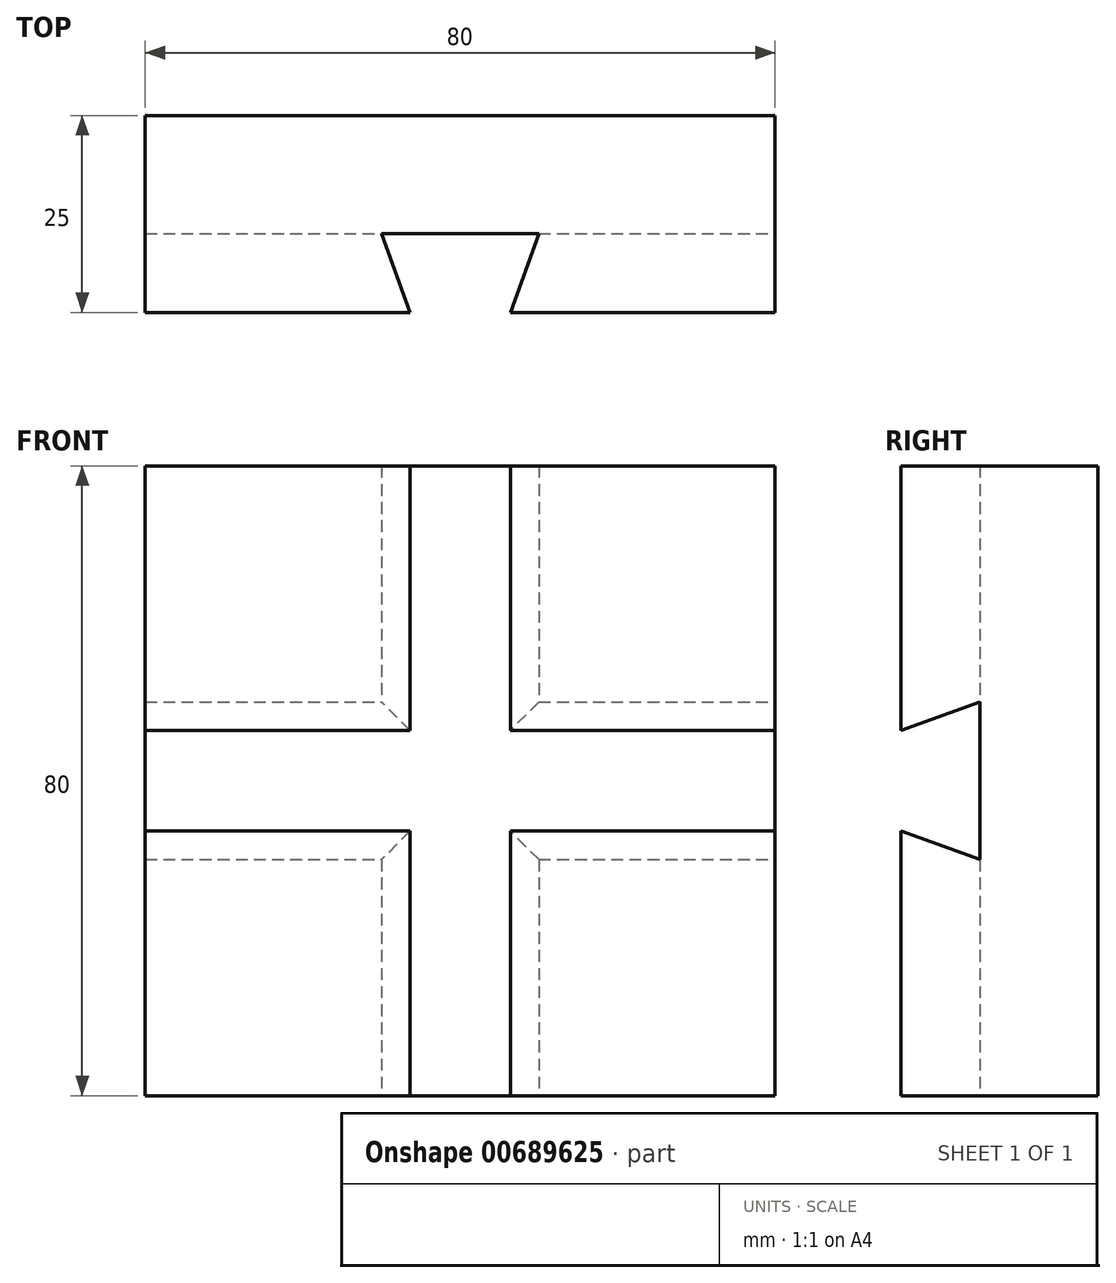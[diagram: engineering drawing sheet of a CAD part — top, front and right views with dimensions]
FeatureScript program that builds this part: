
annotation { "Feature Type Name" : "Feature", "Feature Type Description" : "" }
export const myFeature = defineFeature(function(context is Context, id is Id, definition is map)
    precondition{}
    {
        {
            var Q0;
            Q0=qCreatedBy(makeId("Front.planeOp"),FACE);
            var sketch = newSketch(context, id + "F0", { "sketchPlane" : qUnion([Q0])});
            skLineSegment(sketch, "E0.bottom", {"start": v(0, 0) * mm, "end": v(-80, 0) * mm});
            skLineSegment(sketch, "E0.top", {"start": v(0, 80) * mm, "end": v(-80, 80) * mm});
            skLineSegment(sketch, "E0.left", {"start": v(0, 0) * mm, "end": v(0, 80) * mm});
            skLineSegment(sketch, "E0.right", {"start": v(-80, 0) * mm, "end": v(-80, 80) * mm});
            skLineSegment(sketch, "E1", {"start": v(0, 0) * mm, "end": v(0, 33.64) * mm});
            skSolve(sketch);
        }
        {
            var Q0;
            Q0=makeQuery(id+"F0.imprint","IMPRINT",FACE,{"disambiguationData":[TD([[makeQuery(id+"F0.imprint","IMPRINT",EDGE,{"derivedFrom":sQuery(id+"F0.wireOp",EDGE,"E0.bottom")}),-1.0]])]});
            extrude(context, id + "F1", {"entities" : qUnion([Q0]), "depth" : 25 * mm, "offsetDistance" : 25 * mm});
        }
        {
            var Q0;
            Q0=makeQuery(id+"F1.opExtrude","SWEPT_FACE",FACE,{"disambiguationData":[OSD([sQuery(id+"F0.wireOp",EDGE,"E0.bottom")])]});
            var sketch = newSketch(context, id + "F2", { "sketchPlane" : qUnion([Q0])});
            skLineSegment(sketch, "E2", {"start": v(-46.36, 25) * mm, "end": v(-33.64, 25) * mm});
            skLineSegment(sketch, "E3", {"start": v(-50, 15) * mm, "end": v(-30, 15) * mm});
            skLineSegment(sketch, "E4", {"start": v(-50, 15) * mm, "end": v(-46.36, 25) * mm});
            skLineSegment(sketch, "E5", {"start": v(-33.64, 25) * mm, "end": v(-30, 15) * mm});
            skSolve(sketch);
        }
        {
            var Q0;
            Q0=makeQuery(id+"F2.imprint","IMPRINT",FACE,{"disambiguationData":[TD([[makeQuery(id+"F2.imprint","IMPRINT",EDGE,{"derivedFrom":sQuery(id+"F2.wireOp",EDGE,"E2")}),1.0]])]});
            extrude(context, id + "F3", {"entities" : qUnion([Q0]), "operationType" : NewBodyOperationType.REMOVE, "oppositeDirection" : true, "depth" : 80 * mm, "offsetDistance" : 25 * mm});
        }
        {
            var Q0;
            Q0=qCreatedBy(makeId("Right.planeOp"),FACE);
            var sketch = newSketch(context, id + "F4", { "sketchPlane" : qUnion([Q0])});
            skLineSegment(sketch, "E6", {"start": v(-15, 30) * mm, "end": v(-15, 50) * mm});
            skLineSegment(sketch, "E7", {"start": v(-25.11, 33.64) * mm, "end": v(-25.11, 46.36) * mm});
            skLineSegment(sketch, "E8", {"start": v(-25.11, 33.64) * mm, "end": v(-15, 30) * mm});
            skLineSegment(sketch, "E9", {"start": v(-25.11, 46.36) * mm, "end": v(-15, 50) * mm});
            skSolve(sketch);
        }
        {
            var Q0;
            Q0=makeQuery(id+"F4.imprint","IMPRINT",FACE,{"disambiguationData":[TD([[makeQuery(id+"F4.imprint","IMPRINT",EDGE,{"derivedFrom":sQuery(id+"F4.wireOp",EDGE,"E6")}),1.0]])]});
            extrude(context, id + "F5", {"entities" : qUnion([Q0]), "operationType" : NewBodyOperationType.REMOVE, "oppositeDirection" : true, "depth" : 80 * mm, "offsetDistance" : 25 * mm});
        }
    });
